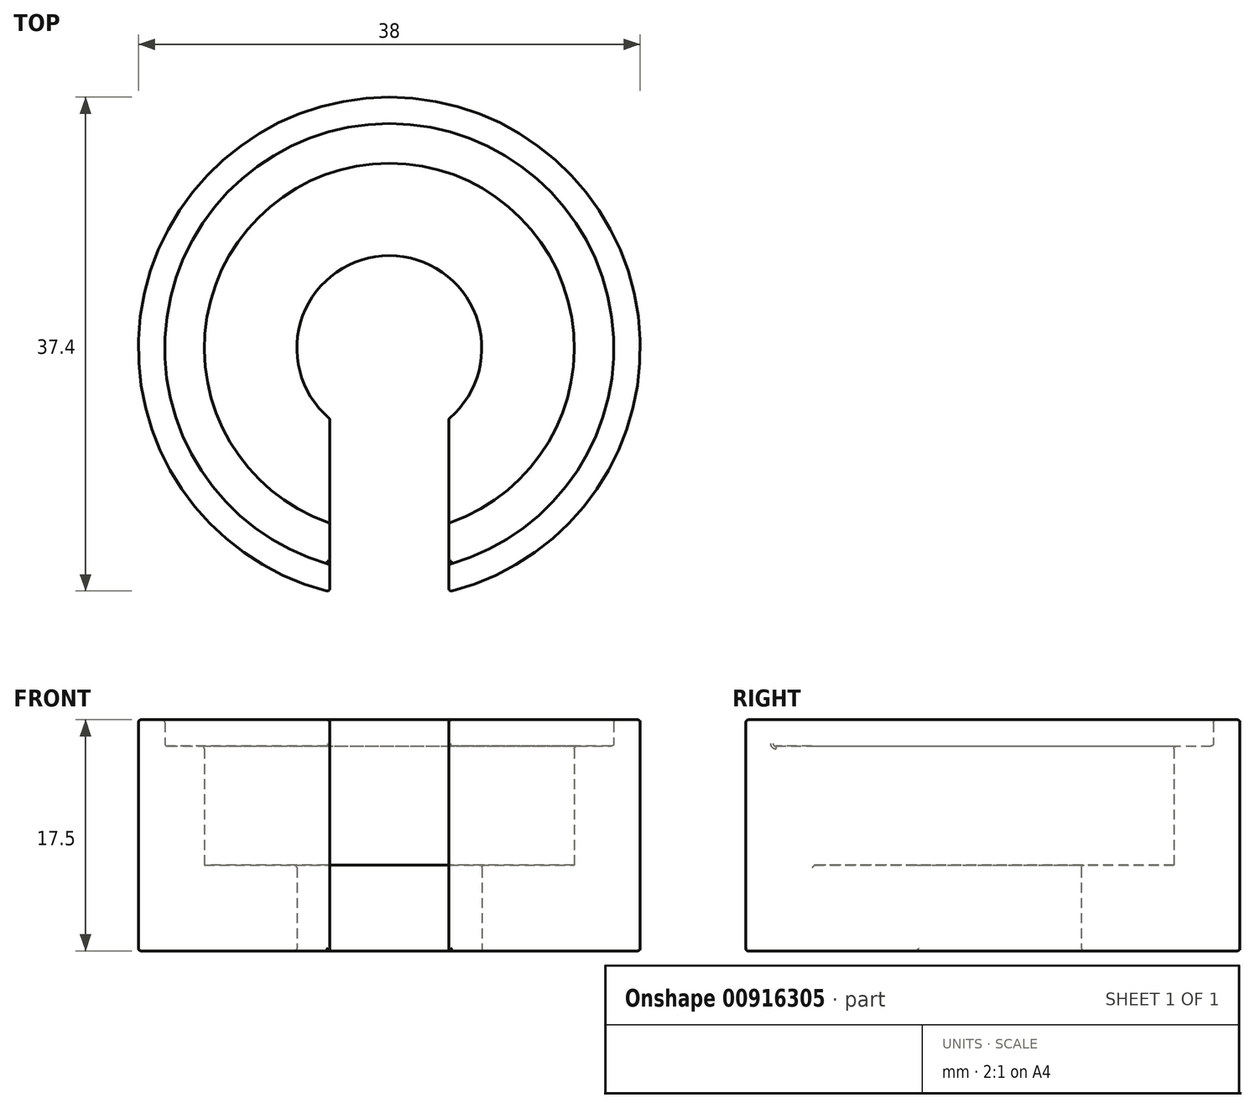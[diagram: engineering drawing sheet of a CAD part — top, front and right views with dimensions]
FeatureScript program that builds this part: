
annotation { "Feature Type Name" : "Feature", "Feature Type Description" : "" }
export const myFeature = defineFeature(function(context is Context, id is Id, definition is map)
    precondition{}
    {
        {
            var Q0;
            Q0=qCreatedBy(makeId("Front.planeOp"),FACE);
            var sketch = newSketch(context, id + "F0", { "sketchPlane" : qUnion([Q0])});
            skLineSegment(sketch, "E0", {"start": v(7, 0) * mm, "end": v(7, 6.5) * mm});
            skLineSegment(sketch, "E1", {"start": v(7, 6.5) * mm, "end": v(14, 6.5) * mm});
            skLineSegment(sketch, "E2", {"start": v(14, 6.5) * mm, "end": v(14, 15.5) * mm});
            skLineSegment(sketch, "E3", {"start": v(14, 15.5) * mm, "end": v(17, 15.5) * mm});
            skLineSegment(sketch, "E4", {"start": v(17, 15.5) * mm, "end": v(17, 17.5) * mm});
            skLineSegment(sketch, "E5", {"start": v(17, 17.5) * mm, "end": v(19, 17.5) * mm});
            skLineSegment(sketch, "E6", {"start": v(19, 17.5) * mm, "end": v(19, 0) * mm});
            skLineSegment(sketch, "E7", {"start": v(19, 0) * mm, "end": v(7, 0) * mm});
            skSolve(sketch);
        }
        {
            var Q0;
            Q0=qCreatedBy(makeId("Top.planeOp"),FACE);
            var sketch = newSketch(context, id + "F1", { "sketchPlane" : qUnion([Q0])});
            skCircle(sketch, "E8", {"center": v(0, 0) * mm, "radius": 14.17 * mm, "construction": true});
            skLineSegment(sketch, "E9.bottom", {"start": v(4.5, -0.93) * mm, "end": v(-4.5, -0.93) * mm});
            skLineSegment(sketch, "E9.top", {"start": v(4.5, -27.41) * mm, "end": v(-4.5, -27.41) * mm});
            skLineSegment(sketch, "E9.left", {"start": v(4.5, -0.93) * mm, "end": v(4.5, -27.41) * mm});
            skLineSegment(sketch, "E9.right", {"start": v(-4.5, -0.93) * mm, "end": v(-4.5, -27.41) * mm});
            skPoint(sketch, "E9.middle", {"position": v(0, -14.17) * mm});
            skSolve(sketch);
        }
        {
            var Q0;
            Q0=makeQuery(id+"F0.imprint","IMPRINT",FACE,{"disambiguationData":[TD([[makeQuery(id+"F0.imprint","IMPRINT",EDGE,{"derivedFrom":sQuery(id+"F0.wireOp",EDGE,"E0")}),-1.0]])]});
            var Q1;
            Q1=sQuery(id+"F1.wireOp",EDGE,"E8");
            revolve(context, id + "F2", {"surfaceOperationType" : NewSurfaceOperationType.NEW, "entities" : qUnion([Q0]), "axis" : qUnion([Q1]), "revolveType" : RevolveType.FULL});
        }
        {
            var Q0;
            Q0=makeQuery(id+"F1.imprint","IMPRINT",FACE,{"disambiguationData":[TD([[makeQuery(id+"F1.imprint","IMPRINT",EDGE,{"derivedFrom":sQuery(id+"F1.wireOp",EDGE,"E9.bottom")}),1.0]])]});
            extrude(context, id + "F3", {"entities" : qUnion([Q0]), "operationType" : NewBodyOperationType.REMOVE, "depth" : 76.9 * mm, "offsetDistance" : 25 * mm});
        }
        {
            var Q0;
            Q0=makeQuery(id+"F2.opRevolve","SWEPT_EDGE",EDGE,{"disambiguationData":[OSD([sQuery(id+"F0.wireOp",EDGE,"E5"),sQuery(id+"F0.wireOp",EDGE,"E6")])]});
            var Q1;
            Q1=makeQuery(id+"F2.opRevolve","SWEPT_EDGE",EDGE,{"disambiguationData":[OSD([sQuery(id+"F0.wireOp",EDGE,"E4"),sQuery(id+"F0.wireOp",EDGE,"E5")])]});
            var Q2;
            Q2=makeQuery(id+"F2.opRevolve","SWEPT_EDGE",EDGE,{"disambiguationData":[OSD([sQuery(id+"F0.wireOp",EDGE,"E2"),sQuery(id+"F0.wireOp",EDGE,"E3")])]});
            var Q3;
            Q3=makeQuery(id+"F2.opRevolve","SWEPT_EDGE",EDGE,{"disambiguationData":[OSD([sQuery(id+"F0.wireOp",EDGE,"E6"),sQuery(id+"F0.wireOp",EDGE,"E7")])]});
            var Q4;
            Q4=makeQuery(id+"F2.opRevolve","SWEPT_EDGE",EDGE,{"disambiguationData":[OSD([sQuery(id+"F0.wireOp",EDGE,"E0"),sQuery(id+"F0.wireOp",EDGE,"E1")])]});
            var Q5;
            Q5=makeQuery(id+"F3.boolean.opBoolean","INTERSECT",EDGE,{"derivedFrom":[makeQuery(id+"F2.opRevolve","SWEPT_FACE",FACE,{"disambiguationData":[OSD([sQuery(id+"F0.wireOp",EDGE,"E6")])]}),makeQuery(id+"F3.opExtrude","SWEPT_FACE",FACE,{"disambiguationData":[OSD([sQuery(id+"F1.wireOp",EDGE,"E9.left")])]})]});
            var Q6;
            Q6=makeQuery(id+"F3.boolean.opBoolean","INTERSECT",EDGE,{"derivedFrom":[makeQuery(id+"F2.opRevolve","SWEPT_FACE",FACE,{"disambiguationData":[OSD([sQuery(id+"F0.wireOp",EDGE,"E6")])]}),makeQuery(id+"F3.opExtrude","SWEPT_FACE",FACE,{"disambiguationData":[OSD([sQuery(id+"F1.wireOp",EDGE,"E9.right")])]})]});
            var Q7;
            Q7=makeQuery(id+"F3.boolean.opBoolean","INTERSECT",EDGE,{"derivedFrom":[makeQuery(id+"F2.opRevolve","SWEPT_FACE",FACE,{"disambiguationData":[OSD([sQuery(id+"F0.wireOp",EDGE,"E2")])]}),makeQuery(id+"F3.opExtrude","SWEPT_FACE",FACE,{"disambiguationData":[OSD([sQuery(id+"F1.wireOp",EDGE,"E9.left")])]})]});
            var Q8;
            Q8=makeQuery(id+"F3.boolean.opBoolean","INTERSECT",EDGE,{"derivedFrom":[makeQuery(id+"F2.opRevolve","SWEPT_FACE",FACE,{"disambiguationData":[OSD([sQuery(id+"F0.wireOp",EDGE,"E1")])]}),makeQuery(id+"F3.opExtrude","SWEPT_FACE",FACE,{"disambiguationData":[OSD([sQuery(id+"F1.wireOp",EDGE,"E9.left")])]})]});
            var Q9;
            Q9=makeQuery(id+"F3.boolean.opBoolean","INTERSECT",EDGE,{"derivedFrom":[makeQuery(id+"F2.opRevolve","SWEPT_FACE",FACE,{"disambiguationData":[OSD([sQuery(id+"F0.wireOp",EDGE,"E1")])]}),makeQuery(id+"F3.opExtrude","SWEPT_FACE",FACE,{"disambiguationData":[OSD([sQuery(id+"F1.wireOp",EDGE,"E9.right")])]})]});
            var Q10;
            Q10=makeQuery(id+"F3.boolean.opBoolean","INTERSECT",EDGE,{"derivedFrom":[makeQuery(id+"F2.opRevolve","SWEPT_FACE",FACE,{"disambiguationData":[OSD([sQuery(id+"F0.wireOp",EDGE,"E4")])]}),makeQuery(id+"F3.opExtrude","SWEPT_FACE",FACE,{"disambiguationData":[OSD([sQuery(id+"F1.wireOp",EDGE,"E9.right")])]})]});
            var Q11;
            Q11=makeQuery(id+"F3.boolean.opBoolean","COPY",EDGE,{"derivedFrom":makeQuery(id+"F3.opExtrude","CAP_EDGE",EDGE,{"disambiguationData":[OSD([sQuery(id+"F1.wireOp",EDGE,"E9.right")])],"isStart":true})});
            var Q12;
            Q12=makeQuery(id+"F3.boolean.opBoolean","INTERSECT",EDGE,{"derivedFrom":[makeQuery(id+"F2.opRevolve","SWEPT_FACE",FACE,{"disambiguationData":[OSD([sQuery(id+"F0.wireOp",EDGE,"E2")])]}),makeQuery(id+"F3.opExtrude","SWEPT_FACE",FACE,{"disambiguationData":[OSD([sQuery(id+"F1.wireOp",EDGE,"E9.right")])]})]});
            var Q13;
            Q13=makeQuery(id+"F2.opRevolve","SWEPT_EDGE",EDGE,{"disambiguationData":[OSD([sQuery(id+"F0.wireOp",EDGE,"E3"),sQuery(id+"F0.wireOp",EDGE,"E4")])]});
            var Q14;
            Q14=makeQuery(id+"F3.boolean.opBoolean","INTERSECT",EDGE,{"derivedFrom":[makeQuery(id+"F2.opRevolve","SWEPT_FACE",FACE,{"disambiguationData":[OSD([sQuery(id+"F0.wireOp",EDGE,"E5")])]}),makeQuery(id+"F3.opExtrude","SWEPT_FACE",FACE,{"disambiguationData":[OSD([sQuery(id+"F1.wireOp",EDGE,"E9.left")])]})]});
            var Q15;
            Q15=makeQuery(id+"F2.opRevolve","SWEPT_EDGE",EDGE,{"disambiguationData":[OSD([sQuery(id+"F0.wireOp",EDGE,"E0"),sQuery(id+"F0.wireOp",EDGE,"E7")])]});
            var Q16;
            Q16=makeQuery(id+"F3.boolean.opBoolean","INTERSECT",EDGE,{"derivedFrom":[makeQuery(id+"F2.opRevolve","SWEPT_FACE",FACE,{"disambiguationData":[OSD([sQuery(id+"F0.wireOp",EDGE,"E0")])]}),makeQuery(id+"F3.opExtrude","SWEPT_FACE",FACE,{"disambiguationData":[OSD([sQuery(id+"F1.wireOp",EDGE,"E9.right")])]})]});
            var Q17;
            Q17=makeQuery(id+"F3.boolean.opBoolean","COPY",EDGE,{"derivedFrom":makeQuery(id+"F3.opExtrude","CAP_EDGE",EDGE,{"disambiguationData":[OSD([sQuery(id+"F1.wireOp",EDGE,"E9.left")])],"isStart":true})});
            var Q18;
            Q18=makeQuery(id+"F3.boolean.opBoolean","INTERSECT",EDGE,{"derivedFrom":[makeQuery(id+"F2.opRevolve","SWEPT_FACE",FACE,{"disambiguationData":[OSD([sQuery(id+"F0.wireOp",EDGE,"E3")])]}),makeQuery(id+"F3.opExtrude","SWEPT_FACE",FACE,{"disambiguationData":[OSD([sQuery(id+"F1.wireOp",EDGE,"E9.right")])]})]});
            var Q19;
            Q19=makeQuery(id+"F3.boolean.opBoolean","INTERSECT",EDGE,{"derivedFrom":[makeQuery(id+"F2.opRevolve","SWEPT_FACE",FACE,{"disambiguationData":[OSD([sQuery(id+"F0.wireOp",EDGE,"E0")])]}),makeQuery(id+"F3.opExtrude","SWEPT_FACE",FACE,{"disambiguationData":[OSD([sQuery(id+"F1.wireOp",EDGE,"E9.left")])]})]});
            var Q20;
            Q20=makeQuery(id+"F3.boolean.opBoolean","INTERSECT",EDGE,{"derivedFrom":[makeQuery(id+"F2.opRevolve","SWEPT_FACE",FACE,{"disambiguationData":[OSD([sQuery(id+"F0.wireOp",EDGE,"E3")])]}),makeQuery(id+"F3.opExtrude","SWEPT_FACE",FACE,{"disambiguationData":[OSD([sQuery(id+"F1.wireOp",EDGE,"E9.left")])]})]});
            var Q21;
            Q21=makeQuery(id+"F3.boolean.opBoolean","INTERSECT",EDGE,{"derivedFrom":[makeQuery(id+"F2.opRevolve","SWEPT_FACE",FACE,{"disambiguationData":[OSD([sQuery(id+"F0.wireOp",EDGE,"E4")])]}),makeQuery(id+"F3.opExtrude","SWEPT_FACE",FACE,{"disambiguationData":[OSD([sQuery(id+"F1.wireOp",EDGE,"E9.left")])]})]});
            var Q22;
            Q22=makeQuery(id+"F3.boolean.opBoolean","INTERSECT",EDGE,{"derivedFrom":[makeQuery(id+"F2.opRevolve","SWEPT_FACE",FACE,{"disambiguationData":[OSD([sQuery(id+"F0.wireOp",EDGE,"E5")])]}),makeQuery(id+"F3.opExtrude","SWEPT_FACE",FACE,{"disambiguationData":[OSD([sQuery(id+"F1.wireOp",EDGE,"E9.right")])]})]});
            fillet(context, id + "F4", {"entities" : qUnion([Q0, Q1, Q2, Q3, Q4, Q5, Q6, Q7, Q8, Q9, Q10, Q11, Q12, Q13, Q14, Q15, Q16, Q17, Q18, Q19, Q20, Q21, Q22]), "radius" : 0.2 * mm, "tangentPropagation" : true, "allowEdgeOverflow" : false});
        }
    });
